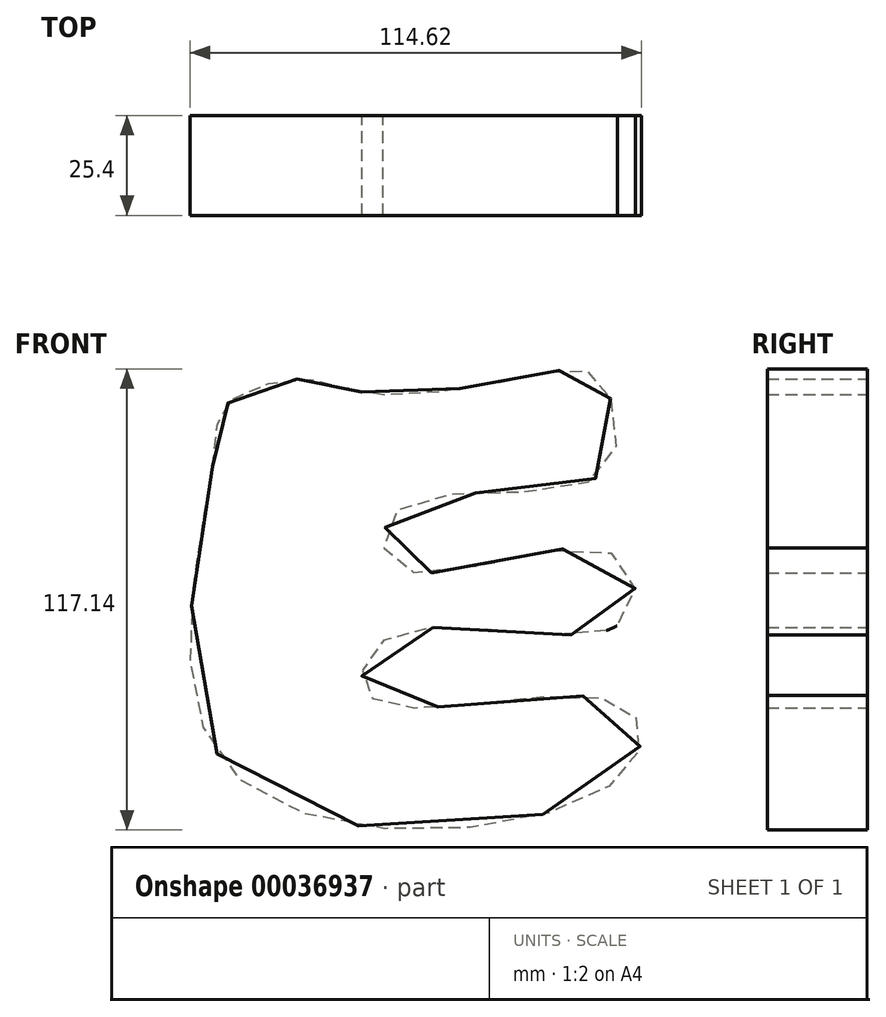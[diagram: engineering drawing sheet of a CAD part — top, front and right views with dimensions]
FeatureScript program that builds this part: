
annotation { "Feature Type Name" : "Feature", "Feature Type Description" : "" }
export const myFeature = defineFeature(function(context is Context, id is Id, definition is map)
    precondition{}
    {
        {
            var Q0;
            Q0=qCreatedBy(makeId("Front.planeOp"),FACE);
            var sketch = newSketch(context, id + "F0", { "sketchPlane" : qUnion([Q0])});
            skFitSpline(sketch, "E0", {"points": [v(-40.79, 7.84) * mm, v(-36.8, 24.1) * mm, v(-17.11, 30.1) * mm, v(0, 26.38) * mm, v(41.93, 31.23) * mm, v(57.62, 29.8) * mm, v(57.9, 5.85) * mm, v(6.85, -2.7) * mm, v(6.85, -18.11) * mm, v(60.47, -14.12) * mm, v(62.75, -32.09) * mm, v(4.56, -35.23) * mm, v(0, -51.2) * mm, v(61.9, -52.06) * mm, v(62.75, -71.17) * mm, v(-35.66, -70.03) * mm, v(-40.79, 7.84) * mm]});
            skSolve(sketch);
        }
        {
            var Q0;
            Q0=makeQuery(id+"F0.imprint","IMPRINT",FACE,{"disambiguationData":[TD([[makeQuery(id+"F0.imprint","IMPRINT",EDGE,{"derivedFrom":sQuery(id+"F0.wireOp",EDGE,"E0")}),-1.0]])]});
            extrude(context, id + "F1", {"entities" : qUnion([Q0]), "depth" : 25.4 * mm});
        }
    });
